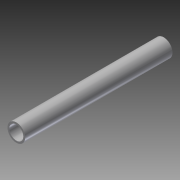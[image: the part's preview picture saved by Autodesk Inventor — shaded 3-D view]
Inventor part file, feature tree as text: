
AUTODESK INVENTOR PART (.ipt)
format: ipt  version: 2013 (Build 170138000, 138)  size: 72,704 bytes
history: native  units: in
note: dims shown in document units (in); Inventor stores cm internally (conversion verified against a paired STEP export)
features: extrude x1, sketch x1
ambient origin geometry x8: Origin, YZ Plane, XZ Plane, XY Plane, X Axis, Y Axis, Z Axis, Center Point
bodies: Solid1 (feature_tree)
feature tree (2):
  extrude  "Extrusion1"  Depth=1.05in
  sketch  "Sketch1"  dims[d0=1.32in d2=1.05in d3=11.0in d4=0.0in]
